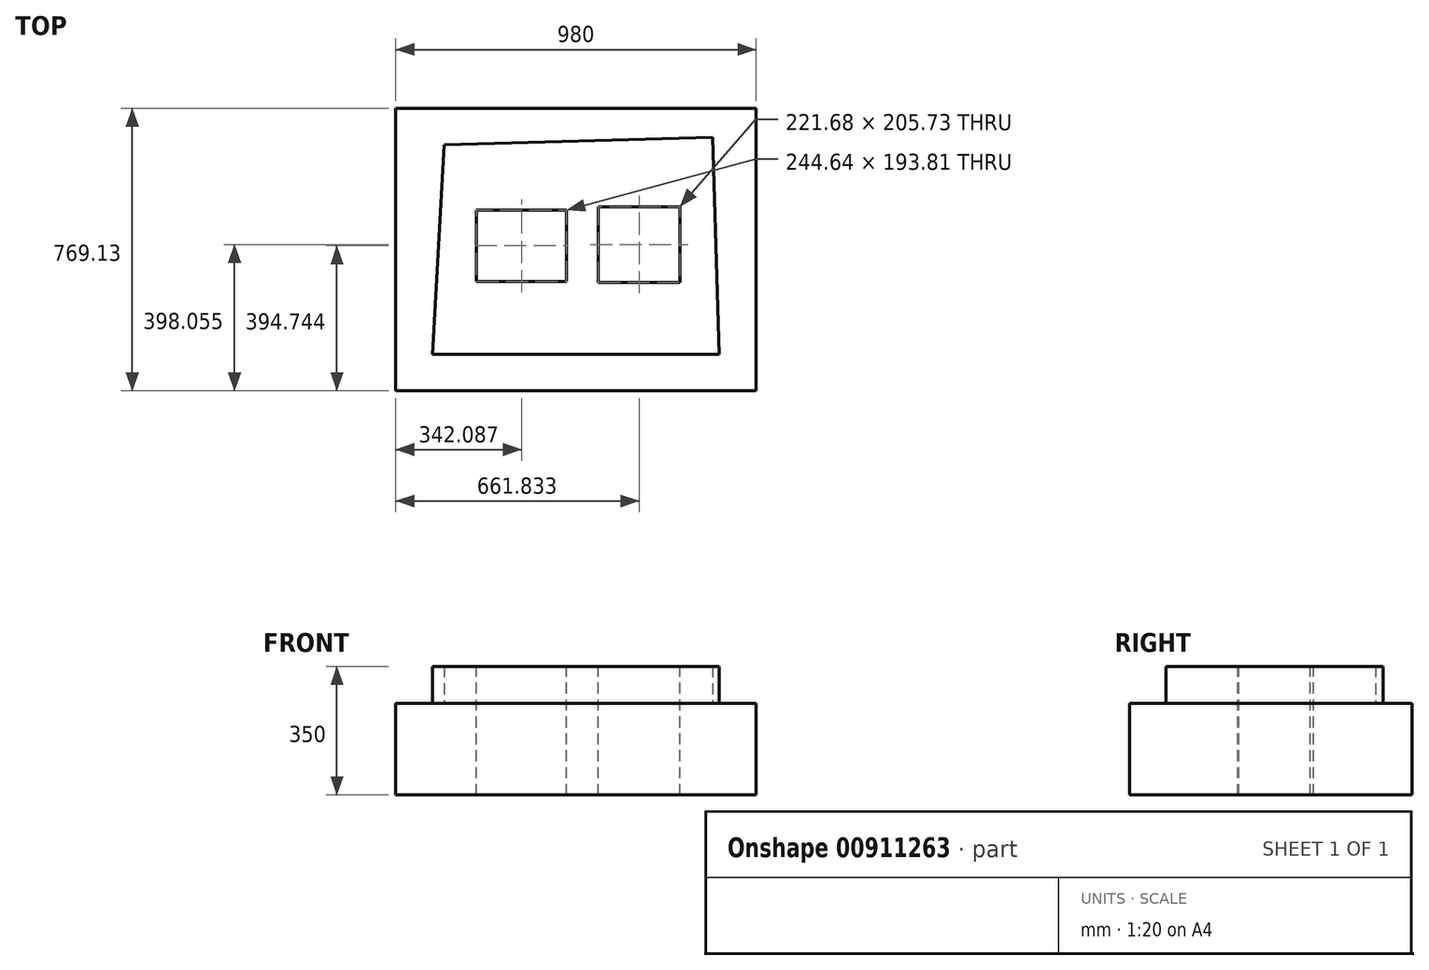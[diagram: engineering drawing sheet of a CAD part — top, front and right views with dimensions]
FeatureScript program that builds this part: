
annotation { "Feature Type Name" : "Feature", "Feature Type Description" : "" }
export const myFeature = defineFeature(function(context is Context, id is Id, definition is map)
    precondition{}
    {
        {
            var Q0;
            Q0=qCreatedBy(makeId("Top.planeOp"),FACE);
            var sketch = newSketch(context, id + "F0", { "sketchPlane" : qUnion([Q0])});
            skLineSegment(sketch, "E0", {"start": v(0, 0) * mm, "end": v(-780, 0) * mm});
            skLineSegment(sketch, "E1", {"start": v(-780, 0) * mm, "end": v(-748.44, 569.13) * mm});
            skLineSegment(sketch, "E2", {"start": v(-748.44, 569.13) * mm, "end": v(-18.73, 589.7) * mm});
            skLineSegment(sketch, "E3", {"start": v(-18.73, 589.7) * mm, "end": v(0, 0) * mm});
            skSolve(sketch);
        }
        {
            var Q0;
            Q0 = qSketchRegion(id + "F0", true);
            extrude(context, id + "F1", {"entities" : qUnion([Q0]), "depth" : 100 * mm, "offsetDistance" : 25 * mm});
        }
        {
            var Q0;
            Q0=makeQuery(id+"F1.opExtrude","CAP_FACE",FACE,{"disambiguationData":[OSD([sQuery(id+"F0.wireOp",EDGE,"E0"),sQuery(id+"F0.wireOp",EDGE,"E1"),sQuery(id+"F0.wireOp",EDGE,"E2"),sQuery(id+"F0.wireOp",EDGE,"E3")])],"isStart":true});
            var sketch = newSketch(context, id + "F2", { "sketchPlane" : qUnion([Q0])});
            skLineSegment(sketch, "E4.bottom", {"start": v(100, 100) * mm, "end": v(-880, 100) * mm});
            skLineSegment(sketch, "E4.top", {"start": v(100, -669.13) * mm, "end": v(-880, -669.13) * mm});
            skLineSegment(sketch, "E4.left", {"start": v(100, 100) * mm, "end": v(100, -669.13) * mm});
            skLineSegment(sketch, "E4.right", {"start": v(-880, 100) * mm, "end": v(-880, -669.13) * mm});
            skSolve(sketch);
        }
        {
            var Q0;
            Q0 = qSketchRegion(id + "F2", true);
            extrude(context, id + "F3", {"entities" : qUnion([Q0]), "operationType" : NewBodyOperationType.ADD, "depth" : 250 * mm, "offsetDistance" : 25 * mm});
        }
        {
            var Q0;
            Q0=makeQuery(id+"F1.opExtrude","CAP_FACE",FACE,{"disambiguationData":[OSD([sQuery(id+"F0.wireOp",EDGE,"E0"),sQuery(id+"F0.wireOp",EDGE,"E1"),sQuery(id+"F0.wireOp",EDGE,"E2"),sQuery(id+"F0.wireOp",EDGE,"E3")])],"isStart":false});
            var sketch = newSketch(context, id + "F4", { "sketchPlane" : qUnion([Q0])});
            skLineSegment(sketch, "E5", {"start": v(-9.37, 294.85) * mm, "end": v(-763.65, 294.85) * mm, "construction": true});
            skLineSegment(sketch, "E6.bottom", {"start": v(-660.23, 391.65) * mm, "end": v(-415.6, 391.65) * mm});
            skLineSegment(sketch, "E6.top", {"start": v(-660.23, 197.84) * mm, "end": v(-415.6, 197.84) * mm});
            skLineSegment(sketch, "E6.left", {"start": v(-660.23, 391.65) * mm, "end": v(-660.23, 197.84) * mm});
            skLineSegment(sketch, "E6.right", {"start": v(-415.6, 391.65) * mm, "end": v(-415.6, 197.84) * mm});
            skLineSegment(sketch, "E7.bottom", {"start": v(-329, 400.92) * mm, "end": v(-107.33, 400.92) * mm});
            skLineSegment(sketch, "E7.top", {"start": v(-329, 195.2) * mm, "end": v(-107.33, 195.2) * mm});
            skLineSegment(sketch, "E7.left", {"start": v(-329, 400.92) * mm, "end": v(-329, 195.2) * mm});
            skLineSegment(sketch, "E7.right", {"start": v(-107.33, 400.92) * mm, "end": v(-107.33, 195.2) * mm});
            skSolve(sketch);
        }
        {
            var Q0;
            Q0 = qSketchRegion(id + "F4", true);
            var Q1;
            Q1=sQuery(id+"F4.wireOp",EDGE,"E6.left");
            extrude(context, id + "F5", {"entities" : qUnion([Q0]), "operationType" : NewBodyOperationType.REMOVE, "surfaceEntities" : qUnion([Q1]), "oppositeDirection" : true, "depth" : 600 * mm, "offsetDistance" : 25 * mm});
        }
    });
